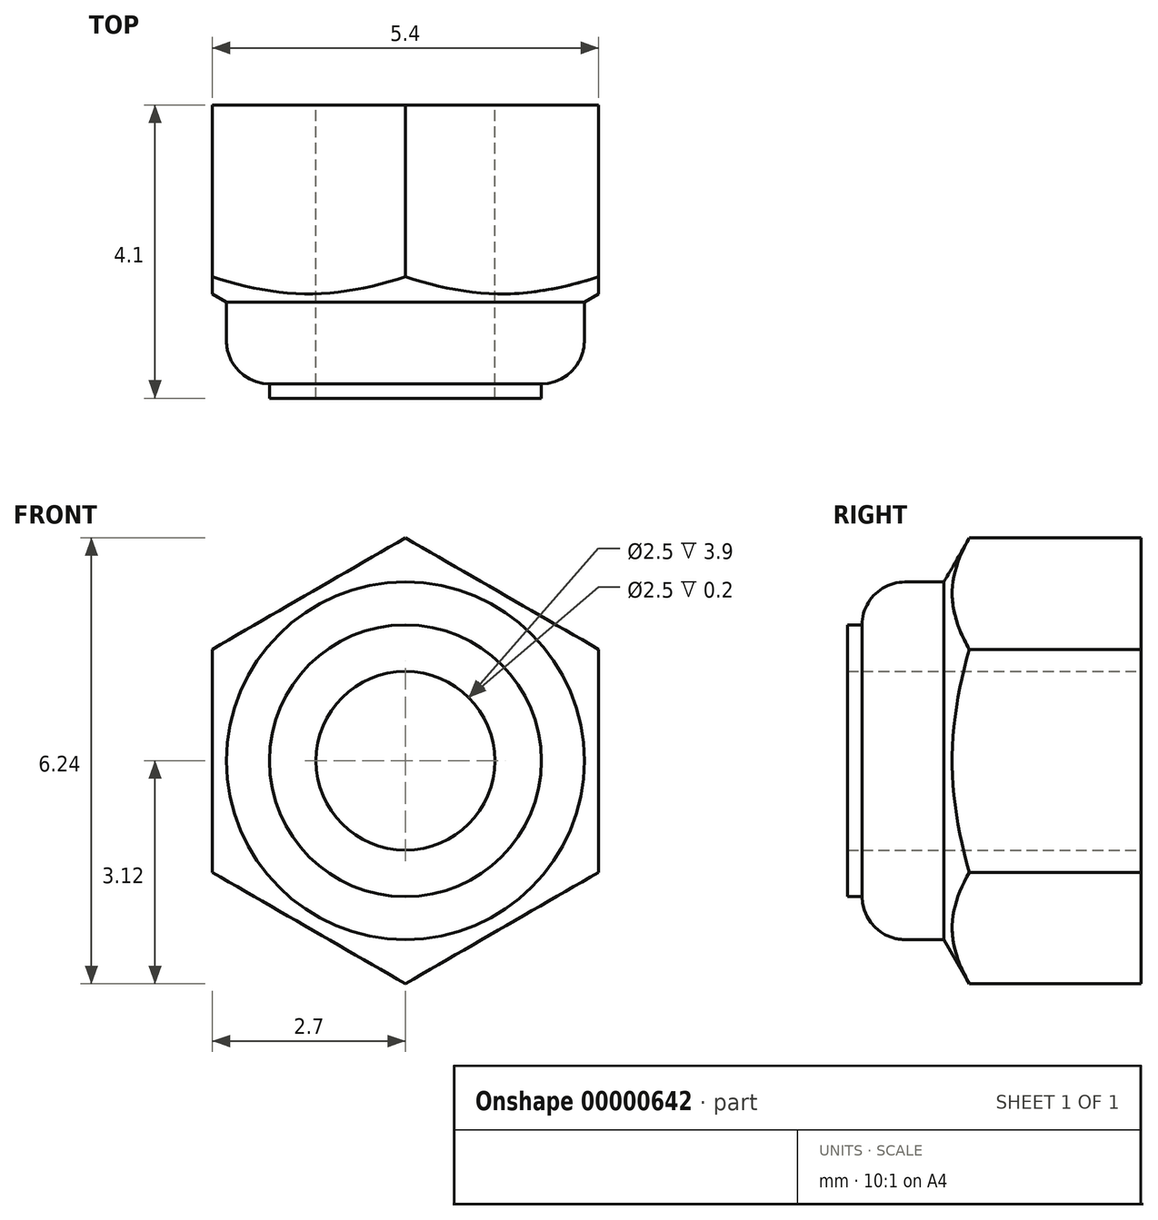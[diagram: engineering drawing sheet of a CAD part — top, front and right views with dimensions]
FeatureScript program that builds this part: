
annotation { "Feature Type Name" : "Feature", "Feature Type Description" : "" }
export const myFeature = defineFeature(function(context is Context, id is Id, definition is map)
    precondition{}
    {
        {
            var Q0;
            Q0 = qCreatedBy(makeId("Front.planeOp"), FACE);
            var sketch = newSketch(context, id + "F0", { "sketchPlane" : qUnion([Q0])});
            skCircle(sketch, "E0.cCircle", {"center": v(0, 0) * mm, "radius": 2.7 * mm, "construction": true});
            skLineSegment(sketch, "E0.0", {"start": v(2.7, 1.56) * mm, "end": v(2.7, -1.56) * mm});
            skLineSegment(sketch, "E0.1", {"start": v(2.7, -1.56) * mm, "end": v(0, -3.12) * mm});
            skLineSegment(sketch, "E0.2", {"start": v(0, -3.12) * mm, "end": v(-2.7, -1.56) * mm});
            skLineSegment(sketch, "E0.3", {"start": v(-2.7, -1.56) * mm, "end": v(-2.7, 1.56) * mm});
            skLineSegment(sketch, "E0.4", {"start": v(-2.7, 1.56) * mm, "end": v(0, 3.12) * mm});
            skLineSegment(sketch, "E0.5", {"start": v(0, 3.12) * mm, "end": v(2.7, 1.56) * mm});
            skPoint(sketch, "E0.0.midPoint", {"position": v(2.7, 0) * mm});
            skSolve(sketch);
        }
        {
            var Q0;
            Q0=makeQuery(id+"F0.imprint","IMPRINT",FACE,{"disambiguationData":[TD([[makeQuery(id+"F0.imprint","IMPRINT",EDGE,{"derivedFrom":sQuery(id+"F0.wireOp",EDGE,"E0.0")}),-1.0]])]});
            extrude(context, id + "F1", {"entities" : qUnion([Q0]), "depth" : 3 * mm});
        }
        {
            var Q0;
            Q0 = qCreatedBy(makeId("Right.planeOp"), FACE);
            var sketch = newSketch(context, id + "F2", { "sketchPlane" : qUnion([Q0])});
            skLineSegment(sketch, "E1", {"start": v(-2.4, 3.12) * mm, "end": v(-4.2, 0) * mm});
            skLineSegment(sketch, "E2", {"start": v(-4.2, 0) * mm, "end": v(-12.28, 0) * mm});
            skLineSegment(sketch, "E3", {"start": v(-12.28, 0) * mm, "end": v(-12.28, 3.12) * mm});
            skLineSegment(sketch, "E4", {"start": v(-2.4, 3.12) * mm, "end": v(-12.28, 3.12) * mm});
            skLineSegment(sketch, "E5", {"start": v(-4.2, 0) * mm, "end": v(3.9, 0) * mm, "construction": true});
            skSolve(sketch);
        }
        {
            var Q0;
            Q0=makeQuery(id+"F2.imprint","IMPRINT",FACE,{"disambiguationData":[TD([[makeQuery(id+"F2.imprint","IMPRINT",EDGE,{"derivedFrom":sQuery(id+"F2.wireOp",EDGE,"E1")}),-1.0]])]});
            var Q1;
            Q1=sQuery(id+"F2.wireOp",EDGE,"E5");
            revolve(context, id + "F3", {"operationType" : NewBodyOperationType.REMOVE, "entities" : qUnion([Q0]), "axis" : qUnion([Q1]), "revolveType" : RevolveType.FULL, "oppositeDirection" : true});
        }
        {
            var Q0;
            Q0=makeQuery(id+"F1.opExtrude","CAP_FACE",FACE,{"disambiguationData":[OSD([sQuery(id+"F0.wireOp",EDGE,"E0.0"),sQuery(id+"F0.wireOp",EDGE,"E0.1"),sQuery(id+"F0.wireOp",EDGE,"E0.2"),sQuery(id+"F0.wireOp",EDGE,"E0.3"),sQuery(id+"F0.wireOp",EDGE,"E0.4"),sQuery(id+"F0.wireOp",EDGE,"E0.5")])],"isStart":true});
            var sketch = newSketch(context, id + "F4", { "sketchPlane" : qUnion([Q0])});
            skCircle(sketch, "E6", {"center": v(0, 0) * mm, "radius": 2.5 * mm});
            skSolve(sketch);
        }
        {
            var Q0;
            Q0=makeQuery(id+"F4.imprint","IMPRINT",FACE,{"disambiguationData":[TD([[makeQuery(id+"F4.imprint","IMPRINT",EDGE,{"derivedFrom":sQuery(id+"F4.wireOp",EDGE,"E6")}),1.0]])]});
            extrude(context, id + "F5", {"entities" : qUnion([Q0]), "operationType" : NewBodyOperationType.ADD, "oppositeDirection" : true, "depth" : 3.9 * mm});
        }
        {
            var Q0;
            Q0=makeQuery(id+"F5.opExtrude","CAP_EDGE",EDGE,{"disambiguationData":[OSD([sQuery(id+"F4.wireOp",EDGE,"E6")])],"isStart":false});
            fillet(context, id + "F6", {"entities" : qUnion([Q0]), "radius" : .6 * mm, "tangentPropagation" : true, "allowEdgeOverflow" : false});
        }
        {
            var Q0;
            Q0=makeQuery(id+"F5.opExtrude","CAP_FACE",FACE,{"disambiguationData":[OSD([sQuery(id+"F4.wireOp",EDGE,"E6")])],"isStart":false});
            var sketch = newSketch(context, id + "F7", { "sketchPlane" : qUnion([Q0])});
            skCircle(sketch, "E7.0", {"center": v(0, 0) * mm, "radius": 1.9 * mm});
            skSolve(sketch);
        }
        {
            var Q0;
            Q0=makeQuery(id+"F7.imprint","IMPRINT",FACE,{"disambiguationData":[TD([[makeQuery(id+"F7.imprint","IMPRINT",EDGE,{"derivedFrom":sQuery(id+"F7.wireOp",EDGE,"E7.0")}),1.0]])]});
            extrude(context, id + "F8", {"entities" : qUnion([Q0]), "depth" : .2 * mm});
        }
        {
            var Q0;
            Q0=makeQuery(id+"F1.opExtrude","CAP_FACE",FACE,{"disambiguationData":[OSD([sQuery(id+"F0.wireOp",EDGE,"E0.0"),sQuery(id+"F0.wireOp",EDGE,"E0.1"),sQuery(id+"F0.wireOp",EDGE,"E0.2"),sQuery(id+"F0.wireOp",EDGE,"E0.3"),sQuery(id+"F0.wireOp",EDGE,"E0.4"),sQuery(id+"F0.wireOp",EDGE,"E0.5")])],"isStart":true});
            var sketch = newSketch(context, id + "F9", { "sketchPlane" : qUnion([Q0])});
            skCircle(sketch, "E8", {"center": v(0, 0) * mm, "radius": 1.25 * mm});
            skSolve(sketch);
        }
        {
            var Q0;
            Q0=makeQuery(id+"F9.imprint","IMPRINT",FACE,{"disambiguationData":[TD([[makeQuery(id+"F9.imprint","IMPRINT",EDGE,{"derivedFrom":sQuery(id+"F9.wireOp",EDGE,"E8")}),1.0]])]});
            extrude(context, id + "F10", {"entities" : qUnion([Q0]), "operationType" : NewBodyOperationType.REMOVE, "oppositeDirection" : true, "depth" : 25 * mm});
        }
    });
